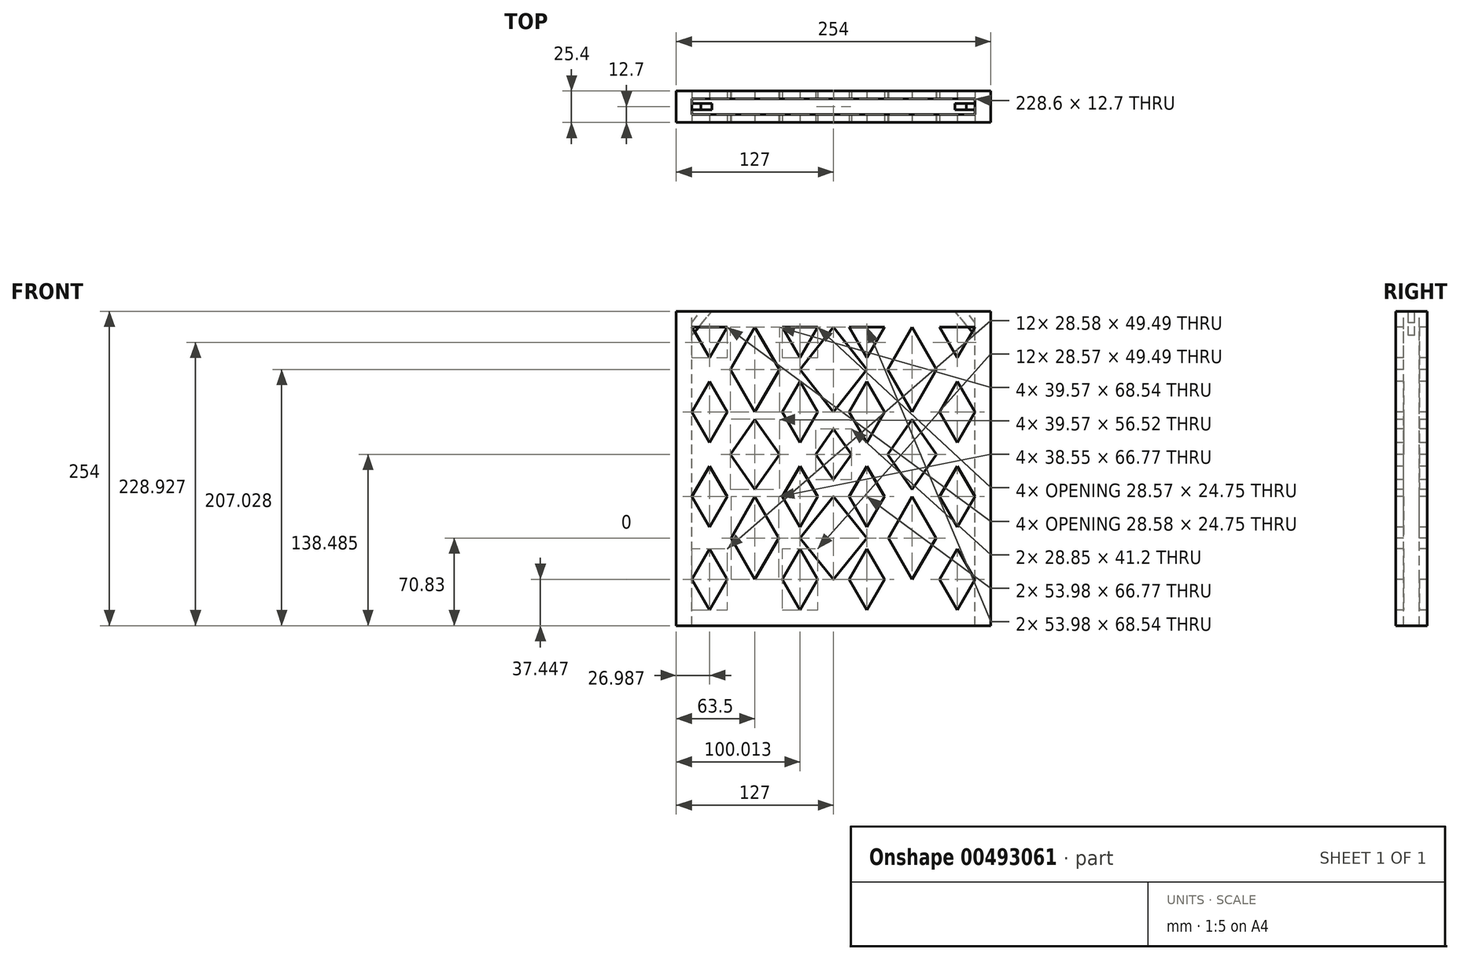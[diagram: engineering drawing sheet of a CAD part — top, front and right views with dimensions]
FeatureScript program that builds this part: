
annotation { "Feature Type Name" : "Feature", "Feature Type Description" : "" }
export const myFeature = defineFeature(function(context is Context, id is Id, definition is map)
    precondition{}
    {
        {
            var Q0;
            Q0=qCreatedBy(makeId("Front.planeOp"),FACE);
            var sketch = newSketch(context, id + "F0", { "sketchPlane" : qUnion([Q0])});
            skLineSegment(sketch, "E0.bottom", {"start": v(127, 127) * mm, "end": v(-127, 127) * mm});
            skLineSegment(sketch, "E0.top", {"start": v(127, -127) * mm, "end": v(-127, -127) * mm});
            skLineSegment(sketch, "E0.left", {"start": v(127, 127) * mm, "end": v(127, -127) * mm});
            skLineSegment(sketch, "E0.right", {"start": v(-127, 127) * mm, "end": v(-127, -127) * mm});
            skPoint(sketch, "E0.middle", {"position": v(0, 0) * mm});
            skSolve(sketch);
        }
        {
            var Q0;
            Q0 = qSketchRegion(id + "F0", true);
            extrude(context, id + "F1", {"entities" : qUnion([Q0]), "depth" : 25.4 * mm, "symmetric" : true});
        }
        {
            var Q0;
            Q0=makeQuery(id+"F1.opExtrude","SWEPT_FACE",FACE,{"disambiguationData":[OSD([sQuery(id+"F0.wireOp",EDGE,"E0.bottom")])]});
            var sketch = newSketch(context, id + "F2", { "sketchPlane" : qUnion([Q0])});
            skPoint(sketch, "E1.0", {"position": v(0, 0) * mm});
            skLineSegment(sketch, "E2.bottom", {"start": v(114.3, 6.35) * mm, "end": v(-114.3, 6.35) * mm});
            skLineSegment(sketch, "E2.top", {"start": v(114.3, -6.35) * mm, "end": v(-114.3, -6.35) * mm});
            skLineSegment(sketch, "E2.left", {"start": v(114.3, 6.35) * mm, "end": v(114.3, -6.35) * mm});
            skLineSegment(sketch, "E2.right", {"start": v(-114.3, 6.35) * mm, "end": v(-114.3, -6.35) * mm});
            skSolve(sketch);
        }
        {
            var Q0;
            Q0 = qSketchRegion(id + "F2", true);
            extrude(context, id + "F3", {"entities" : qUnion([Q0]), "operationType" : NewBodyOperationType.REMOVE, "oppositeDirection" : true, "depth" : 254 * mm});
        }
        {
            var Q0;
            Q0=makeQuery(id+"F1.opExtrude","CAP_FACE",FACE,{"disambiguationData":[OSD([sQuery(id+"F0.wireOp",EDGE,"E0.bottom"),sQuery(id+"F0.wireOp",EDGE,"E0.top"),sQuery(id+"F0.wireOp",EDGE,"E0.left"),sQuery(id+"F0.wireOp",EDGE,"E0.right")])],"isStart":false});
            var sketch = newSketch(context, id + "F4", { "sketchPlane" : qUnion([Q0])});
            skLineSegment(sketch, "E3", {"start": v(127, 127) * mm, "end": v(-127, 127) * mm, "construction": true});
            skLineSegment(sketch, "E4", {"start": v(-127, 127) * mm, "end": v(0, 127) * mm, "construction": true});
            skLineSegment(sketch, "E5", {"start": v(0, 127) * mm, "end": v(0, 0) * mm, "construction": true});
            skLineSegment(sketch, "E6", {"start": v(0, 0) * mm, "end": v(0, -127) * mm, "construction": true});
            skLineSegment(sketch, "E7", {"start": v(0, -127) * mm, "end": v(127, -127) * mm, "construction": true});
            skLineSegment(sketch, "E8", {"start": v(127, -127) * mm, "end": v(-127, -127) * mm, "construction": true});
            skLineSegment(sketch, "E9", {"start": v(114.3, 114.3) * mm, "end": v(100.01, 89.55) * mm});
            skLineSegment(sketch, "E10", {"start": v(100.01, 89.55) * mm, "end": v(85.72, 114.3) * mm});
            skLineSegment(sketch, "E11", {"start": v(85.72, 114.3) * mm, "end": v(114.3, 114.3) * mm});
            skLineSegment(sketch, "E12", {"start": v(114.3, 45.76) * mm, "end": v(85.72, 45.76) * mm});
            skLineSegment(sketch, "E13", {"start": v(85.72, 45.76) * mm, "end": v(100.01, 21) * mm});
            skLineSegment(sketch, "E14", {"start": v(100.01, 21) * mm, "end": v(114.3, 45.76) * mm});
            skLineSegment(sketch, "E15.MirrorCS", {"start": v(85.72, 45.76) * mm, "end": v(100.01, 70.5) * mm});
            skLineSegment(sketch, "E16.MirrorCS", {"start": v(100.01, 70.5) * mm, "end": v(114.3, 45.76) * mm});
            skLineSegment(sketch, "E17", {"start": v(100.01, 1.96) * mm, "end": v(114.3, -22.79) * mm});
            skLineSegment(sketch, "E18", {"start": v(114.3, -22.79) * mm, "end": v(85.73, -22.79) * mm});
            skLineSegment(sketch, "E19", {"start": v(85.72, -22.79) * mm, "end": v(100.01, 1.96) * mm});
            skLineSegment(sketch, "E20.MirrorCS", {"start": v(100.01, -47.53) * mm, "end": v(114.3, -22.79) * mm});
            skLineSegment(sketch, "E21.MirrorCS", {"start": v(85.72, -22.79) * mm, "end": v(100.01, -47.53) * mm});
            skLineSegment(sketch, "E22", {"start": v(114.3, -89.55) * mm, "end": v(100.01, -64.8) * mm});
            skLineSegment(sketch, "E23", {"start": v(100.01, -64.8) * mm, "end": v(85.72, -89.55) * mm});
            skLineSegment(sketch, "E24", {"start": v(114.3, -89.55) * mm, "end": v(85.72, -89.55) * mm});
            skLineSegment(sketch, "E25", {"start": v(63.5, -127) * mm, "end": v(63.5, 127) * mm, "construction": true});
            skLineSegment(sketch, "E26.MirrorCS", {"start": v(100.01, -114.3) * mm, "end": v(85.72, -89.55) * mm});
            skLineSegment(sketch, "E27.MirrorCS", {"start": v(114.3, -89.55) * mm, "end": v(100.01, -114.3) * mm});
            skLineSegment(sketch, "E28.MirrorCS", {"start": v(12.7, -89.55) * mm, "end": v(41.28, -89.55) * mm});
            skLineSegment(sketch, "E29.MirrorCS", {"start": v(41.28, 45.76) * mm, "end": v(26.99, 70.5) * mm});
            skLineSegment(sketch, "E30.MirrorCS", {"start": v(26.99, -47.53) * mm, "end": v(12.7, -22.79) * mm});
            skLineSegment(sketch, "E31.MirrorCS", {"start": v(12.7, -89.55) * mm, "end": v(26.99, -64.8) * mm});
            skLineSegment(sketch, "E32.MirrorCS", {"start": v(26.99, 1.96) * mm, "end": v(12.7, -22.79) * mm});
            skLineSegment(sketch, "E33.MirrorCS", {"start": v(12.7, -22.79) * mm, "end": v(41.28, -22.79) * mm});
            skLineSegment(sketch, "E34.MirrorCS", {"start": v(26.99, 70.5) * mm, "end": v(12.7, 45.76) * mm});
            skLineSegment(sketch, "E35.MirrorCS", {"start": v(12.7, -89.55) * mm, "end": v(26.99, -114.3) * mm});
            skLineSegment(sketch, "E36.MirrorCS", {"start": v(41.28, -22.79) * mm, "end": v(26.99, -47.53) * mm});
            skLineSegment(sketch, "E37.MirrorCS", {"start": v(26.99, -64.8) * mm, "end": v(41.28, -89.55) * mm});
            skLineSegment(sketch, "E38.MirrorCS", {"start": v(41.28, -22.79) * mm, "end": v(26.99, 1.96) * mm});
            skLineSegment(sketch, "E39.MirrorCS", {"start": v(12.7, 45.76) * mm, "end": v(41.28, 45.76) * mm});
            skLineSegment(sketch, "E40.MirrorCS", {"start": v(41.28, 45.76) * mm, "end": v(26.99, 21) * mm});
            skLineSegment(sketch, "E41.MirrorCS", {"start": v(26.99, 21) * mm, "end": v(12.7, 45.76) * mm});
            skLineSegment(sketch, "E42.MirrorCS", {"start": v(41.28, 114.3) * mm, "end": v(12.7, 114.3) * mm});
            skLineSegment(sketch, "E43.MirrorCS", {"start": v(26.99, 89.55) * mm, "end": v(41.28, 114.3) * mm});
            skLineSegment(sketch, "E44.MirrorCS", {"start": v(26.99, -114.3) * mm, "end": v(41.28, -89.55) * mm});
            skLineSegment(sketch, "E45.MirrorCS", {"start": v(12.7, 114.3) * mm, "end": v(26.99, 89.55) * mm});
            skLineSegment(sketch, "E46.MirrorCS", {"start": v(-127, -127) * mm, "end": v(127, -127) * mm, "construction": true});
            skLineSegment(sketch, "E47.MirrorCS", {"start": v(-114.3, -89.55) * mm, "end": v(-85.72, -89.55) * mm});
            skLineSegment(sketch, "E48.MirrorCS", {"start": v(-85.72, 45.76) * mm, "end": v(-100.01, 70.5) * mm});
            skLineSegment(sketch, "E49.MirrorCS", {"start": v(-41.28, 45.76) * mm, "end": v(-26.99, 70.5) * mm});
            skLineSegment(sketch, "E50.MirrorCS", {"start": v(-12.7, -22.79) * mm, "end": v(-41.28, -22.79) * mm});
            skLineSegment(sketch, "E51.MirrorCS", {"start": v(-41.28, 45.76) * mm, "end": v(-26.99, 21) * mm});
            skLineSegment(sketch, "E52.MirrorCS", {"start": v(-26.99, 70.5) * mm, "end": v(-12.7, 45.76) * mm});
            skLineSegment(sketch, "E53.MirrorCS", {"start": v(-26.99, -114.3) * mm, "end": v(-41.28, -89.55) * mm});
            skLineSegment(sketch, "E54.MirrorCS", {"start": v(-12.7, -89.55) * mm, "end": v(-26.99, -64.8) * mm});
            skLineSegment(sketch, "E55.MirrorCS", {"start": v(-41.28, -22.79) * mm, "end": v(-26.99, 1.96) * mm});
            skLineSegment(sketch, "E56.MirrorCS", {"start": v(-114.3, -22.79) * mm, "end": v(-85.72, -22.79) * mm});
            skLineSegment(sketch, "E57.MirrorCS", {"start": v(-114.3, -89.55) * mm, "end": v(-100.01, -64.8) * mm});
            skLineSegment(sketch, "E58.MirrorCS", {"start": v(-100.01, 70.5) * mm, "end": v(-114.3, 45.76) * mm});
            skLineSegment(sketch, "E59.MirrorCS", {"start": v(-100.01, 1.96) * mm, "end": v(-114.3, -22.79) * mm});
            skLineSegment(sketch, "E60.MirrorCS", {"start": v(-114.3, 114.3) * mm, "end": v(-100.01, 89.55) * mm});
            skLineSegment(sketch, "E61.MirrorCS", {"start": v(-100.01, 89.55) * mm, "end": v(-85.73, 114.3) * mm});
            skLineSegment(sketch, "E62.MirrorCS", {"start": v(-85.73, 114.3) * mm, "end": v(-114.3, 114.3) * mm});
            skLineSegment(sketch, "E63.MirrorCS", {"start": v(-26.99, 89.55) * mm, "end": v(-41.28, 114.3) * mm});
            skLineSegment(sketch, "E64.MirrorCS", {"start": v(-100.01, -47.53) * mm, "end": v(-114.3, -22.79) * mm});
            skLineSegment(sketch, "E65.MirrorCS", {"start": v(-41.28, -22.79) * mm, "end": v(-26.99, -47.53) * mm});
            skLineSegment(sketch, "E66.MirrorCS", {"start": v(-114.3, -89.55) * mm, "end": v(-100.01, -114.3) * mm});
            skLineSegment(sketch, "E67.MirrorCS", {"start": v(-41.28, 114.3) * mm, "end": v(-12.7, 114.3) * mm});
            skLineSegment(sketch, "E68.MirrorCS", {"start": v(-26.99, -47.53) * mm, "end": v(-12.7, -22.79) * mm});
            skLineSegment(sketch, "E69.MirrorCS", {"start": v(-100.01, 21) * mm, "end": v(-114.3, 45.76) * mm});
            skLineSegment(sketch, "E70.MirrorCS", {"start": v(-26.99, 21) * mm, "end": v(-12.7, 45.76) * mm});
            skLineSegment(sketch, "E71.MirrorCS", {"start": v(-12.7, -89.55) * mm, "end": v(-41.28, -89.55) * mm});
            skLineSegment(sketch, "E72.MirrorCS", {"start": v(-12.7, 114.3) * mm, "end": v(-26.99, 89.55) * mm});
            skLineSegment(sketch, "E73.MirrorCS", {"start": v(-85.72, 45.76) * mm, "end": v(-100.01, 21) * mm});
            skLineSegment(sketch, "E74.MirrorCS", {"start": v(-12.7, 45.76) * mm, "end": v(-41.28, 45.76) * mm});
            skLineSegment(sketch, "E75.MirrorCS", {"start": v(-26.99, 1.96) * mm, "end": v(-12.7, -22.79) * mm});
            skLineSegment(sketch, "E76.MirrorCS", {"start": v(-100.01, -64.8) * mm, "end": v(-85.72, -89.55) * mm});
            skLineSegment(sketch, "E77.MirrorCS", {"start": v(-12.7, -89.55) * mm, "end": v(-26.99, -114.3) * mm});
            skLineSegment(sketch, "E78.MirrorCS", {"start": v(-26.99, -64.8) * mm, "end": v(-41.28, -89.55) * mm});
            skLineSegment(sketch, "E79.MirrorCS", {"start": v(-114.3, 45.76) * mm, "end": v(-85.72, 45.76) * mm});
            skLineSegment(sketch, "E80.MirrorCS", {"start": v(-85.72, -22.79) * mm, "end": v(-100.01, 1.96) * mm});
            skLineSegment(sketch, "E81.MirrorCS", {"start": v(-85.72, -22.79) * mm, "end": v(-100.01, -47.53) * mm});
            skLineSegment(sketch, "E82.MirrorCS", {"start": v(-100.01, -114.3) * mm, "end": v(-85.72, -89.55) * mm});
            skSolve(sketch);
        }
        {
            var Q0;
            Q0=makeQuery(id+"F4.imprint","IMPRINT",FACE,{"disambiguationData":[TD([[makeQuery(id+"F4.imprint","IMPRINT",EDGE,{"derivedFrom":sQuery(id+"F4.wireOp",EDGE,"E24")}),1.0]])]});
            var Q1;
            Q1=makeQuery(id+"F4.imprint","IMPRINT",FACE,{"disambiguationData":[TD([[makeQuery(id+"F4.imprint","IMPRINT",EDGE,{"derivedFrom":sQuery(id+"F4.wireOp",EDGE,"E22")}),1.0]])]});
            var Q2;
            Q2=makeQuery(id+"F4.imprint","IMPRINT",FACE,{"disambiguationData":[TD([[makeQuery(id+"F4.imprint","IMPRINT",EDGE,{"derivedFrom":sQuery(id+"F4.wireOp",EDGE,"E28.MirrorCS")}),-1.0]])]});
            var Q3;
            Q3=makeQuery(id+"F4.imprint","IMPRINT",FACE,{"disambiguationData":[TD([[makeQuery(id+"F4.imprint","IMPRINT",EDGE,{"derivedFrom":sQuery(id+"F4.wireOp",EDGE,"E28.MirrorCS")}),1.0]])]});
            var Q4;
            Q4=makeQuery(id+"F4.imprint","IMPRINT",FACE,{"disambiguationData":[TD([[makeQuery(id+"F4.imprint","IMPRINT",EDGE,{"derivedFrom":sQuery(id+"F4.wireOp",EDGE,"E53.MirrorCS")}),-1.0]])]});
            var Q5;
            Q5=makeQuery(id+"F4.imprint","IMPRINT",FACE,{"disambiguationData":[TD([[makeQuery(id+"F4.imprint","IMPRINT",EDGE,{"derivedFrom":sQuery(id+"F4.wireOp",EDGE,"E54.MirrorCS")}),1.0]])]});
            var Q6;
            Q6=makeQuery(id+"F4.imprint","IMPRINT",FACE,{"disambiguationData":[TD([[makeQuery(id+"F4.imprint","IMPRINT",EDGE,{"derivedFrom":sQuery(id+"F4.wireOp",EDGE,"E47.MirrorCS")}),-1.0]])]});
            var Q7;
            Q7=makeQuery(id+"F4.imprint","IMPRINT",FACE,{"disambiguationData":[TD([[makeQuery(id+"F4.imprint","IMPRINT",EDGE,{"derivedFrom":sQuery(id+"F4.wireOp",EDGE,"E47.MirrorCS")}),1.0]])]});
            var Q8;
            Q8=makeQuery(id+"F4.imprint","IMPRINT",FACE,{"disambiguationData":[TD([[makeQuery(id+"F4.imprint","IMPRINT",EDGE,{"derivedFrom":sQuery(id+"F4.wireOp",EDGE,"E56.MirrorCS")}),-1.0]])]});
            var Q9;
            Q9=makeQuery(id+"F4.imprint","IMPRINT",FACE,{"disambiguationData":[TD([[makeQuery(id+"F4.imprint","IMPRINT",EDGE,{"derivedFrom":sQuery(id+"F4.wireOp",EDGE,"E56.MirrorCS")}),1.0]])]});
            var Q10;
            Q10=makeQuery(id+"F4.imprint","IMPRINT",FACE,{"disambiguationData":[TD([[makeQuery(id+"F4.imprint","IMPRINT",EDGE,{"derivedFrom":sQuery(id+"F4.wireOp",EDGE,"E50.MirrorCS")}),1.0]])]});
            var Q11;
            Q11=makeQuery(id+"F4.imprint","IMPRINT",FACE,{"disambiguationData":[TD([[makeQuery(id+"F4.imprint","IMPRINT",EDGE,{"derivedFrom":sQuery(id+"F4.wireOp",EDGE,"E50.MirrorCS")}),-1.0]])]});
            var Q12;
            Q12=makeQuery(id+"F4.imprint","IMPRINT",FACE,{"disambiguationData":[TD([[makeQuery(id+"F4.imprint","IMPRINT",EDGE,{"derivedFrom":sQuery(id+"F4.wireOp",EDGE,"E30.MirrorCS")}),-1.0]])]});
            var Q13;
            Q13=makeQuery(id+"F4.imprint","IMPRINT",FACE,{"disambiguationData":[TD([[makeQuery(id+"F4.imprint","IMPRINT",EDGE,{"derivedFrom":sQuery(id+"F4.wireOp",EDGE,"E32.MirrorCS")}),1.0]])]});
            var Q14;
            Q14=makeQuery(id+"F4.imprint","IMPRINT",FACE,{"disambiguationData":[TD([[makeQuery(id+"F4.imprint","IMPRINT",EDGE,{"derivedFrom":sQuery(id+"F4.wireOp",EDGE,"E18")}),1.0]])]});
            var Q15;
            Q15=makeQuery(id+"F4.imprint","IMPRINT",FACE,{"disambiguationData":[TD([[makeQuery(id+"F4.imprint","IMPRINT",EDGE,{"derivedFrom":sQuery(id+"F4.wireOp",EDGE,"E17")}),-1.0]])]});
            var Q16;
            Q16=makeQuery(id+"F4.imprint","IMPRINT",FACE,{"disambiguationData":[TD([[makeQuery(id+"F4.imprint","IMPRINT",EDGE,{"derivedFrom":sQuery(id+"F4.wireOp",EDGE,"E12")}),1.0]])]});
            var Q17;
            Q17=makeQuery(id+"F4.imprint","IMPRINT",FACE,{"disambiguationData":[TD([[makeQuery(id+"F4.imprint","IMPRINT",EDGE,{"derivedFrom":sQuery(id+"F4.wireOp",EDGE,"E12")}),-1.0]])]});
            var Q18;
            Q18=makeQuery(id+"F4.imprint","IMPRINT",FACE,{"disambiguationData":[TD([[makeQuery(id+"F4.imprint","IMPRINT",EDGE,{"derivedFrom":sQuery(id+"F4.wireOp",EDGE,"E39.MirrorCS")}),-1.0]])]});
            var Q19;
            Q19=makeQuery(id+"F4.imprint","IMPRINT",FACE,{"disambiguationData":[TD([[makeQuery(id+"F4.imprint","IMPRINT",EDGE,{"derivedFrom":sQuery(id+"F4.wireOp",EDGE,"E34.MirrorCS")}),1.0]])]});
            var Q20;
            Q20=makeQuery(id+"F4.imprint","IMPRINT",FACE,{"disambiguationData":[TD([[makeQuery(id+"F4.imprint","IMPRINT",EDGE,{"derivedFrom":sQuery(id+"F4.wireOp",EDGE,"E51.MirrorCS")}),1.0]])]});
            var Q21;
            Q21=makeQuery(id+"F4.imprint","IMPRINT",FACE,{"disambiguationData":[TD([[makeQuery(id+"F4.imprint","IMPRINT",EDGE,{"derivedFrom":sQuery(id+"F4.wireOp",EDGE,"E52.MirrorCS")}),-1.0]])]});
            var Q22;
            Q22=makeQuery(id+"F4.imprint","IMPRINT",FACE,{"disambiguationData":[TD([[makeQuery(id+"F4.imprint","IMPRINT",EDGE,{"derivedFrom":sQuery(id+"F4.wireOp",EDGE,"E69.MirrorCS")}),-1.0]])]});
            var Q23;
            Q23=makeQuery(id+"F4.imprint","IMPRINT",FACE,{"disambiguationData":[TD([[makeQuery(id+"F4.imprint","IMPRINT",EDGE,{"derivedFrom":sQuery(id+"F4.wireOp",EDGE,"E58.MirrorCS")}),1.0]])]});
            var Q24;
            Q24=makeQuery(id+"F4.imprint","IMPRINT",FACE,{"disambiguationData":[TD([[makeQuery(id+"F4.imprint","IMPRINT",EDGE,{"derivedFrom":sQuery(id+"F4.wireOp",EDGE,"E60.MirrorCS")}),1.0]])]});
            var Q25;
            Q25=makeQuery(id+"F4.imprint","IMPRINT",FACE,{"disambiguationData":[TD([[makeQuery(id+"F4.imprint","IMPRINT",EDGE,{"derivedFrom":sQuery(id+"F4.wireOp",EDGE,"E63.MirrorCS")}),-1.0]])]});
            var Q26;
            Q26=makeQuery(id+"F4.imprint","IMPRINT",FACE,{"disambiguationData":[TD([[makeQuery(id+"F4.imprint","IMPRINT",EDGE,{"derivedFrom":sQuery(id+"F4.wireOp",EDGE,"E42.MirrorCS")}),1.0]])]});
            var Q27;
            Q27=makeQuery(id+"F4.imprint","IMPRINT",FACE,{"disambiguationData":[TD([[makeQuery(id+"F4.imprint","IMPRINT",EDGE,{"derivedFrom":sQuery(id+"F4.wireOp",EDGE,"E9")}),-1.0]])]});
            extrude(context, id + "F5", {"entities" : qUnion([Q0, Q1, Q2, Q3, Q4, Q5, Q6, Q7, Q8, Q9, Q10, Q11, Q12, Q13, Q14, Q15, Q16, Q17, Q18, Q19, Q20, Q21, Q22, Q23, Q24, Q25, Q26, Q27]), "operationType" : NewBodyOperationType.REMOVE, "oppositeDirection" : true, "depth" : 123.7 * mm});
        }
        {
            var Q0;
            Q0=makeQuery(id+"F1.opExtrude","CAP_FACE",FACE,{"disambiguationData":[OSD([sQuery(id+"F0.wireOp",EDGE,"E0.bottom"),sQuery(id+"F0.wireOp",EDGE,"E0.top"),sQuery(id+"F0.wireOp",EDGE,"E0.left"),sQuery(id+"F0.wireOp",EDGE,"E0.right")])],"isStart":false});
            var sketch = newSketch(context, id + "F6", { "sketchPlane" : qUnion([Q0])});
            skLineSegment(sketch, "E83", {"start": v(-85.73, 114.3) * mm, "end": v(-41.28, 114.3) * mm, "construction": true});
            skLineSegment(sketch, "E84", {"start": v(-41.28, 114.3) * mm, "end": v(-63.5, 114.3) * mm, "construction": true});
            skLineSegment(sketch, "E85", {"start": v(41.28, 114.3) * mm, "end": v(85.72, 114.3) * mm, "construction": true});
            skLineSegment(sketch, "E86", {"start": v(85.72, 114.3) * mm, "end": v(63.5, 114.3) * mm, "construction": true});
            skLineSegment(sketch, "E87", {"start": v(41.28, 45.76) * mm, "end": v(85.72, 45.76) * mm, "construction": true});
            skLineSegment(sketch, "E88", {"start": v(85.72, 45.76) * mm, "end": v(63.5, 45.76) * mm, "construction": true});
            skLineSegment(sketch, "E89", {"start": v(-41.28, 45.76) * mm, "end": v(-85.72, 45.76) * mm, "construction": true});
            skLineSegment(sketch, "E90", {"start": v(-85.72, 45.76) * mm, "end": v(-63.5, 45.76) * mm, "construction": true});
            skLineSegment(sketch, "E91", {"start": v(-85.72, -22.79) * mm, "end": v(-41.28, -22.79) * mm, "construction": true});
            skLineSegment(sketch, "E92", {"start": v(-41.28, -22.79) * mm, "end": v(-63.5, -22.79) * mm, "construction": true});
            skLineSegment(sketch, "E93", {"start": v(41.28, -22.79) * mm, "end": v(85.73, -22.79) * mm, "construction": true});
            skLineSegment(sketch, "E94", {"start": v(85.73, -22.79) * mm, "end": v(63.5, -22.79) * mm, "construction": true});
            skLineSegment(sketch, "E95", {"start": v(-85.72, -89.55) * mm, "end": v(-41.28, -89.55) * mm, "construction": true});
            skLineSegment(sketch, "E96", {"start": v(-41.28, -89.55) * mm, "end": v(-63.5, -89.55) * mm, "construction": true});
            skLineSegment(sketch, "E97", {"start": v(41.28, -89.55) * mm, "end": v(85.72, -89.55) * mm, "construction": true});
            skLineSegment(sketch, "E98", {"start": v(85.72, -89.55) * mm, "end": v(63.5, -89.55) * mm, "construction": true});
            skLineSegment(sketch, "E99", {"start": v(-100.01, 89.55) * mm, "end": v(-100.01, 70.5) * mm, "construction": true});
            skLineSegment(sketch, "E100", {"start": v(-100.01, 70.5) * mm, "end": v(-100.01, 80.03) * mm, "construction": true});
            skLineSegment(sketch, "E101", {"start": v(-26.99, 89.55) * mm, "end": v(-26.99, 70.5) * mm, "construction": true});
            skLineSegment(sketch, "E102", {"start": v(-26.99, 70.5) * mm, "end": v(-26.99, 80.03) * mm, "construction": true});
            skLineSegment(sketch, "E103", {"start": v(26.99, 70.5) * mm, "end": v(26.99, 89.55) * mm, "construction": true});
            skLineSegment(sketch, "E104", {"start": v(26.99, 89.55) * mm, "end": v(26.99, 80.03) * mm, "construction": true});
            skLineSegment(sketch, "E105", {"start": v(100.01, 89.55) * mm, "end": v(100.01, 70.5) * mm, "construction": true});
            skLineSegment(sketch, "E106", {"start": v(100.01, 70.5) * mm, "end": v(100.01, 80.03) * mm, "construction": true});
            skLineSegment(sketch, "E107", {"start": v(-100.01, 80.03) * mm, "end": v(-26.99, 80.03) * mm, "construction": true});
            skLineSegment(sketch, "E108", {"start": v(-63.5, 45.76) * mm, "end": v(-83.29, 80.03) * mm});
            skLineSegment(sketch, "E109", {"start": v(-83.29, 80.03) * mm, "end": v(-63.5, 114.3) * mm});
            skLineSegment(sketch, "E110", {"start": v(-63.5, 114.3) * mm, "end": v(-43.71, 80.03) * mm});
            skLineSegment(sketch, "E111", {"start": v(-43.71, 80.03) * mm, "end": v(-63.5, 45.76) * mm});
            skLineSegment(sketch, "E112.MirrorCS", {"start": v(43.71, 80.03) * mm, "end": v(63.5, 45.76) * mm});
            skLineSegment(sketch, "E113.MirrorCS", {"start": v(63.5, 114.3) * mm, "end": v(43.71, 80.03) * mm});
            skLineSegment(sketch, "E114.MirrorCS", {"start": v(41.28, 114.3) * mm, "end": v(63.5, 114.3) * mm, "construction": true});
            skLineSegment(sketch, "E115.MirrorCS", {"start": v(85.73, 114.3) * mm, "end": v(41.28, 114.3) * mm, "construction": true});
            skLineSegment(sketch, "E116.MirrorCS", {"start": v(83.29, 80.03) * mm, "end": v(63.5, 114.3) * mm});
            skLineSegment(sketch, "E117.MirrorCS", {"start": v(63.5, 45.76) * mm, "end": v(83.29, 80.03) * mm});
            skLineSegment(sketch, "E118.MirrorCS", {"start": v(100.01, 80.03) * mm, "end": v(26.99, 80.03) * mm, "construction": true});
            skLineSegment(sketch, "E119", {"start": v(-73.4, 0) * mm, "end": v(0, 0) * mm, "construction": true});
            skLineSegment(sketch, "E120", {"start": v(0, 0) * mm, "end": v(83.46, 0) * mm, "construction": true});
            skLineSegment(sketch, "E121", {"start": v(-100.01, -47.53) * mm, "end": v(-100.01, -64.8) * mm, "construction": true});
            skLineSegment(sketch, "E122", {"start": v(-26.99, -47.53) * mm, "end": v(-26.99, -64.8) * mm, "construction": true});
            skLineSegment(sketch, "E123", {"start": v(-26.99, -64.8) * mm, "end": v(-26.99, -56.17) * mm, "construction": true});
            skLineSegment(sketch, "E124", {"start": v(-26.99, -56.17) * mm, "end": v(-100.01, -56.17) * mm, "construction": true});
            skLineSegment(sketch, "E125", {"start": v(-63.5, -22.79) * mm, "end": v(-82.77, -56.17) * mm});
            skLineSegment(sketch, "E126", {"start": v(-82.77, -56.17) * mm, "end": v(-63.5, -89.55) * mm});
            skLineSegment(sketch, "E127", {"start": v(-44.23, -56.17) * mm, "end": v(-63.5, -89.55) * mm});
            skLineSegment(sketch, "E128", {"start": v(-44.23, -56.17) * mm, "end": v(-63.5, -22.79) * mm});
            skLineSegment(sketch, "E129.MirrorCS", {"start": v(41.28, -22.79) * mm, "end": v(63.5, -22.79) * mm, "construction": true});
            skLineSegment(sketch, "E130.MirrorCS", {"start": v(41.28, -89.55) * mm, "end": v(63.5, -89.55) * mm, "construction": true});
            skLineSegment(sketch, "E131.MirrorCS", {"start": v(44.23, -56.17) * mm, "end": v(63.5, -22.79) * mm});
            skLineSegment(sketch, "E132.MirrorCS", {"start": v(44.23, -56.17) * mm, "end": v(63.5, -89.55) * mm});
            skLineSegment(sketch, "E133.MirrorCS", {"start": v(63.5, -22.79) * mm, "end": v(82.77, -56.17) * mm});
            skLineSegment(sketch, "E134.MirrorCS", {"start": v(82.77, -56.17) * mm, "end": v(63.5, -89.55) * mm});
            skLineSegment(sketch, "E135", {"start": v(-100.01, 21) * mm, "end": v(-100.01, 1.96) * mm, "construction": true});
            skLineSegment(sketch, "E136", {"start": v(-100.01, 1.96) * mm, "end": v(-100.01, 11.48) * mm, "construction": true});
            skLineSegment(sketch, "E137", {"start": v(-26.99, 21) * mm, "end": v(-26.99, 1.96) * mm, "construction": true});
            skLineSegment(sketch, "E138", {"start": v(-26.99, 1.96) * mm, "end": v(-26.99, 11.48) * mm, "construction": true});
            skLineSegment(sketch, "E139", {"start": v(-100.01, 11.48) * mm, "end": v(-26.99, 11.48) * mm, "construction": true});
            skLineSegment(sketch, "E140", {"start": v(-63.5, 45.76) * mm, "end": v(-63.5, -22.79) * mm, "construction": true});
            skLineSegment(sketch, "E141", {"start": v(-63.5, 39.74) * mm, "end": v(-83.29, 11.48) * mm});
            skLineSegment(sketch, "E142", {"start": v(-83.29, 11.48) * mm, "end": v(-63.5, -16.77) * mm});
            skLineSegment(sketch, "E143", {"start": v(-63.5, -16.77) * mm, "end": v(-43.71, 11.48) * mm});
            skLineSegment(sketch, "E144", {"start": v(-43.71, 11.48) * mm, "end": v(-63.5, 39.74) * mm});
            skLineSegment(sketch, "E145.MirrorCS", {"start": v(63.5, -16.77) * mm, "end": v(43.71, 11.48) * mm});
            skLineSegment(sketch, "E146.MirrorCS", {"start": v(43.71, 11.48) * mm, "end": v(63.5, 39.74) * mm});
            skLineSegment(sketch, "E147.MirrorCS", {"start": v(83.29, 11.48) * mm, "end": v(63.5, -16.77) * mm});
            skLineSegment(sketch, "E148.MirrorCS", {"start": v(63.5, 39.74) * mm, "end": v(83.29, 11.48) * mm});
            skLineSegment(sketch, "E149", {"start": v(-12.7, 114.3) * mm, "end": v(12.7, 114.3) * mm, "construction": true});
            skLineSegment(sketch, "E150", {"start": v(-12.7, 45.76) * mm, "end": v(12.7, 45.76) * mm, "construction": true});
            skLineSegment(sketch, "E151", {"start": v(-12.7, -22.79) * mm, "end": v(12.7, -22.79) * mm, "construction": true});
            skLineSegment(sketch, "E152", {"start": v(-12.7, -89.55) * mm, "end": v(12.7, -89.55) * mm, "construction": true});
            skLineSegment(sketch, "E153", {"start": v(-26.99, 80.03) * mm, "end": v(0, 114.3) * mm});
            skLineSegment(sketch, "E154", {"start": v(0, 114.3) * mm, "end": v(26.99, 80.03) * mm});
            skLineSegment(sketch, "E155", {"start": v(0, 45.76) * mm, "end": v(26.99, 80.03) * mm});
            skLineSegment(sketch, "E156", {"start": v(0, 45.76) * mm, "end": v(-26.99, 80.03) * mm});
            skLineSegment(sketch, "E157", {"start": v(-26.99, 80.03) * mm, "end": v(26.99, 80.03) * mm, "construction": true});
            skLineSegment(sketch, "E158", {"start": v(26.99, -47.53) * mm, "end": v(26.99, -64.8) * mm, "construction": true});
            skLineSegment(sketch, "E159", {"start": v(26.99, 21) * mm, "end": v(26.99, 1.96) * mm, "construction": true});
            skLineSegment(sketch, "E160", {"start": v(0, 45.76) * mm, "end": v(0, -22.79) * mm, "construction": true});
            skLineSegment(sketch, "E161", {"start": v(-26.99, 11.48) * mm, "end": v(26.99, 11.48) * mm, "construction": true});
            skLineSegment(sketch, "E162", {"start": v(0, -9.11) * mm, "end": v(14.42, 11.48) * mm});
            skLineSegment(sketch, "E163", {"start": v(14.42, 11.48) * mm, "end": v(0, 32.08) * mm});
            skLineSegment(sketch, "E164", {"start": v(0, 32.08) * mm, "end": v(-14.42, 11.48) * mm});
            skLineSegment(sketch, "E165", {"start": v(-14.42, 11.48) * mm, "end": v(0, -9.11) * mm});
            skLineSegment(sketch, "E166", {"start": v(0, -22.79) * mm, "end": v(-26.99, -56.17) * mm});
            skLineSegment(sketch, "E167", {"start": v(-26.99, -56.17) * mm, "end": v(0, -89.55) * mm});
            skLineSegment(sketch, "E168", {"start": v(26.99, -56.17) * mm, "end": v(0, -89.55) * mm});
            skLineSegment(sketch, "E169", {"start": v(0, -22.79) * mm, "end": v(26.99, -56.17) * mm});
            skLineSegment(sketch, "E170", {"start": v(-26.99, -56.17) * mm, "end": v(26.99, -56.17) * mm, "construction": true});
            skSolve(sketch);
        }
        {
            var Q0;
            Q0=makeQuery(id+"F6.imprint","IMPRINT",FACE,{"disambiguationData":[TD([[makeQuery(id+"F6.imprint","IMPRINT",EDGE,{"derivedFrom":sQuery(id+"F6.wireOp",EDGE,"E108")}),-1.0]])]});
            var Q1;
            Q1=makeQuery(id+"F6.imprint","IMPRINT",FACE,{"disambiguationData":[TD([[makeQuery(id+"F6.imprint","IMPRINT",EDGE,{"derivedFrom":sQuery(id+"F6.wireOp",EDGE,"E153")}),-1.0]])]});
            var Q2;
            Q2=makeQuery(id+"F6.imprint","IMPRINT",FACE,{"disambiguationData":[TD([[makeQuery(id+"F6.imprint","IMPRINT",EDGE,{"derivedFrom":sQuery(id+"F6.wireOp",EDGE,"E113.MirrorCS")}),1.0]])]});
            var Q3;
            Q3=makeQuery(id+"F6.imprint","IMPRINT",FACE,{"disambiguationData":[TD([[makeQuery(id+"F6.imprint","IMPRINT",EDGE,{"derivedFrom":sQuery(id+"F6.wireOp",EDGE,"E145.MirrorCS")}),-1.0]])]});
            var Q4;
            Q4=makeQuery(id+"F6.imprint","IMPRINT",FACE,{"disambiguationData":[TD([[makeQuery(id+"F6.imprint","IMPRINT",EDGE,{"derivedFrom":sQuery(id+"F6.wireOp",EDGE,"E162")}),1.0]])]});
            var Q5;
            Q5=makeQuery(id+"F6.imprint","IMPRINT",FACE,{"disambiguationData":[TD([[makeQuery(id+"F6.imprint","IMPRINT",EDGE,{"derivedFrom":sQuery(id+"F6.wireOp",EDGE,"E141")}),1.0]])]});
            var Q6;
            Q6=makeQuery(id+"F6.imprint","IMPRINT",FACE,{"disambiguationData":[TD([[makeQuery(id+"F6.imprint","IMPRINT",EDGE,{"derivedFrom":sQuery(id+"F6.wireOp",EDGE,"E125")}),1.0]])]});
            var Q7;
            Q7=makeQuery(id+"F6.imprint","IMPRINT",FACE,{"disambiguationData":[TD([[makeQuery(id+"F6.imprint","IMPRINT",EDGE,{"derivedFrom":sQuery(id+"F6.wireOp",EDGE,"E166")}),1.0]])]});
            var Q8;
            Q8=makeQuery(id+"F6.imprint","IMPRINT",FACE,{"disambiguationData":[TD([[makeQuery(id+"F6.imprint","IMPRINT",EDGE,{"derivedFrom":sQuery(id+"F6.wireOp",EDGE,"E131.MirrorCS")}),-1.0]])]});
            extrude(context, id + "F7", {"entities" : qUnion([Q0, Q1, Q2, Q3, Q4, Q5, Q6, Q7, Q8]), "operationType" : NewBodyOperationType.REMOVE, "oppositeDirection" : true, "depth" : 127 * mm});
        }
        {
            var Q0;
            Q0=makeQuery(id+"F3.boolean.opBoolean","COPY",FACE,{"derivedFrom":makeQuery(id+"F3.opExtrude","SWEPT_FACE",FACE,{"disambiguationData":[OSD([sQuery(id+"F2.wireOp",EDGE,"E2.right")])]})});
            var sketch = newSketch(context, id + "F8", { "sketchPlane" : qUnion([Q0])});
            skCircle(sketch, "E171", {"center": v(0, 112.55) * mm, "radius": 5.08 * mm});
            skSolve(sketch);
        }
        {
            var Q0;
            Q0=makeQuery(id+"F1.opExtrude","SWEPT_FACE",FACE,{"disambiguationData":[OSD([sQuery(id+"F0.wireOp",EDGE,"E0.bottom")])]});
            var sketch = newSketch(context, id + "F9", { "sketchPlane" : qUnion([Q0])});
            skCircle(sketch, "E172", {"center": v(-102.65, 0) * mm, "radius": 4.53 * mm});
            skCircle(sketch, "E173.MirrorC", {"center": v(102.65, 0) * mm, "radius": 4.53 * mm});
            skSolve(sketch);
        }
        {
            var Q0;
            Q0=makeQuery(id+"F1.opExtrude","CAP_FACE",FACE,{"disambiguationData":[OSD([sQuery(id+"F0.wireOp",EDGE,"E0.bottom"),sQuery(id+"F0.wireOp",EDGE,"E0.top"),sQuery(id+"F0.wireOp",EDGE,"E0.left"),sQuery(id+"F0.wireOp",EDGE,"E0.right")])],"isStart":true});
            cPlane(context, id + "F10", {"entities" : qUnion([Q0]), "cplaneType" : CPlaneType.OFFSET, "offset" : 12.7 * mm, "oppositeDirection" : true, "width" : 152.4 * mm, "height" : 152.4 * mm});
        }
        {
            var Q0;
            Q0=qCreatedBy(id+"F10.planeOp",FACE);
            var sketch = newSketch(context, id + "F11", { "sketchPlane" : qUnion([Q0])});
            skPoint(sketch, "E174.0", {"position": v(114.3, 112.55) * mm});
            skPoint(sketch, "E175.0", {"position": v(102.65, 127) * mm});
            skLineSegment(sketch, "E176.0", {"start": v(98.13, 127) * mm, "end": v(107.18, 127) * mm});
            skLineSegment(sketch, "E177.0", {"start": v(114.3, 107.47) * mm, "end": v(114.3, 117.63) * mm});
            skLineSegment(sketch, "E178", {"start": v(114.3, 117.63) * mm, "end": v(107.18, 127) * mm});
            skLineSegment(sketch, "E179", {"start": v(114.3, 107.47) * mm, "end": v(98.13, 127) * mm});
            skLineSegment(sketch, "E180.MirrorCS", {"start": v(-98.13, 127) * mm, "end": v(-107.18, 127) * mm});
            skLineSegment(sketch, "E181.MirrorCS", {"start": v(-114.3, 107.47) * mm, "end": v(-114.3, 117.63) * mm});
            skLineSegment(sketch, "E182.MirrorCS", {"start": v(-114.3, 107.47) * mm, "end": v(-98.13, 127) * mm});
            skLineSegment(sketch, "E183.MirrorCS", {"start": v(-114.3, 117.63) * mm, "end": v(-107.18, 127) * mm});
            skPoint(sketch, "E184.MirrorP", {"position": v(-114.3, 112.55) * mm});
            skPoint(sketch, "E185.MirrorP", {"position": v(-102.65, 127) * mm});
            skSolve(sketch);
        }
        {
            var Q0;
            Q0 = qSketchRegion(id + "F11", true);
            extrude(context, id + "F12", {"entities" : qUnion([Q0]), "operationType" : NewBodyOperationType.ADD, "depth" : 5.08 * mm, "symmetric" : true});
        }
    });
